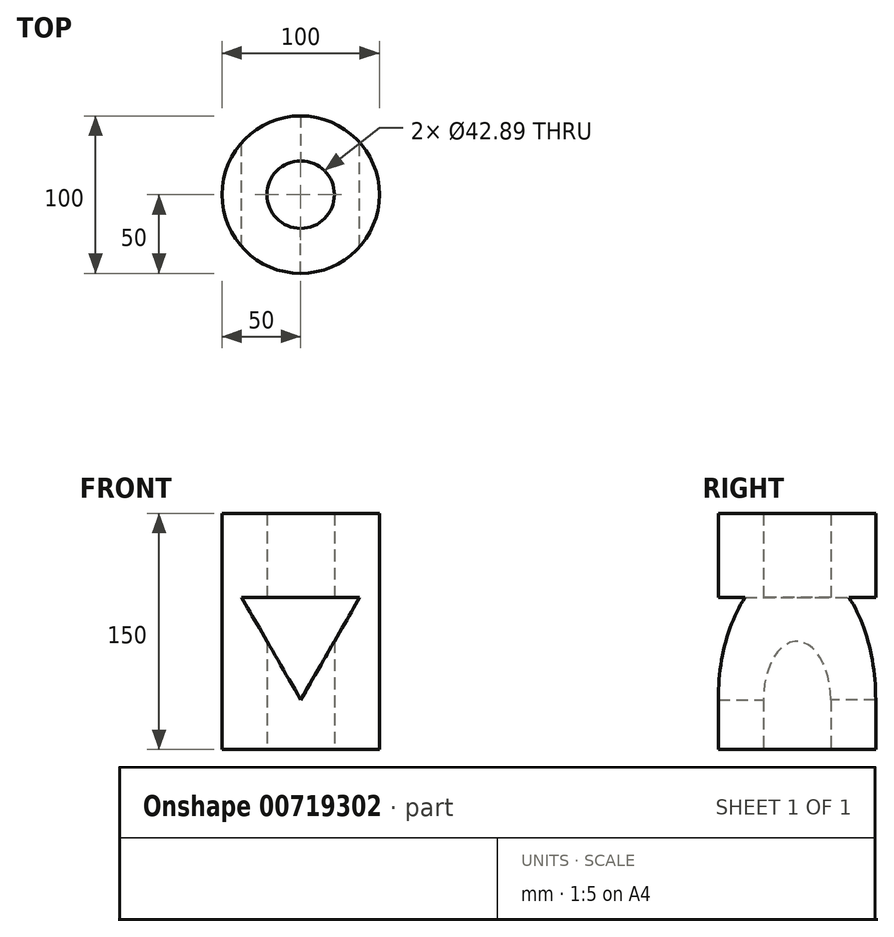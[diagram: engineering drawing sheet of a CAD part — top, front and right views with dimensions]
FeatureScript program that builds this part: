
annotation { "Feature Type Name" : "Feature", "Feature Type Description" : "" }
export const myFeature = defineFeature(function(context is Context, id is Id, definition is map)
    precondition{}
    {
        {
            var Q0;
            Q0=qCreatedBy(makeId("Top.planeOp"),FACE);
            var sketch = newSketch(context, id + "F0", { "sketchPlane" : qUnion([Q0])});
            skCircle(sketch, "E0", {"center": v(0, 0) * mm, "radius": 50 * mm});
            skSolve(sketch);
        }
        {
            var Q0;
            Q0=makeQuery(id+"F0.imprint","IMPRINT",FACE,{"disambiguationData":[TD([[makeQuery(id+"F0.imprint","IMPRINT",EDGE,{"derivedFrom":sQuery(id+"F0.wireOp",EDGE,"E0")}),1.0]])]});
            extrude(context, id + "F1", {"entities" : qUnion([Q0]), "depth" : 150 * mm, "offsetDistance" : 25 * mm});
        }
        {
            var Q0;
            Q0=qCreatedBy(makeId("Top.planeOp"),FACE);
            var sketch = newSketch(context, id + "F2", { "sketchPlane" : qUnion([Q0])});
            skCircle(sketch, "E1", {"center": v(0, 0) * mm, "radius": 21.44 * mm});
            skSolve(sketch);
        }
        {
            var Q0;
            Q0=makeQuery(id+"F2.imprint","IMPRINT",FACE,{"disambiguationData":[TD([[makeQuery(id+"F2.imprint","IMPRINT",EDGE,{"derivedFrom":sQuery(id+"F2.wireOp",EDGE,"E1")}),1.0]])]});
            extrude(context, id + "F3", {"entities" : qUnion([Q0]), "operationType" : NewBodyOperationType.REMOVE, "endBound" : BoundingType.THROUGH_ALL, "depth" : 25 * mm, "offsetDistance" : 25 * mm});
        }
        {
            var Q0;
            Q0=qCreatedBy(makeId("Front.planeOp"),FACE);
            var sketch = newSketch(context, id + "F4", { "sketchPlane" : qUnion([Q0])});
            skCircle(sketch, "E2.cCircle", {"center": v(0, 75) * mm, "radius": 21.65 * mm, "construction": true});
            skLineSegment(sketch, "E2.0", {"start": v(0, 31.7) * mm, "end": v(-37.5, 96.65) * mm});
            skLineSegment(sketch, "E2.1", {"start": v(-37.5, 96.65) * mm, "end": v(37.5, 96.65) * mm});
            skLineSegment(sketch, "E2.2", {"start": v(37.5, 96.65) * mm, "end": v(0, 31.7) * mm});
            skPoint(sketch, "E2.0.midPoint", {"position": v(-20.04, 66.8) * mm});
            skPoint(sketch, "E3", {"position": v(0, 150) * mm});
            skLineSegment(sketch, "E4", {"start": v(0, 150) * mm, "end": v(0, 0) * mm});
            skSolve(sketch);
        }
        {
            var Q0;
            Q0 = qSketchRegion(id + "F4", true);
            extrude(context, id + "F5", {"entities" : qUnion([Q0]), "operationType" : NewBodyOperationType.REMOVE, "endBound" : BoundingType.THROUGH_ALL, "depth" : 25 * mm, "offsetDistance" : 25 * mm});
        }
        {
            var Q0;
            Q0 = qSketchRegion(id + "F4", true);
            extrude(context, id + "F6", {"entities" : qUnion([Q0]), "operationType" : NewBodyOperationType.REMOVE, "endBound" : BoundingType.THROUGH_ALL, "oppositeDirection" : true, "depth" : 25 * mm, "offsetDistance" : 25 * mm});
        }
    });
